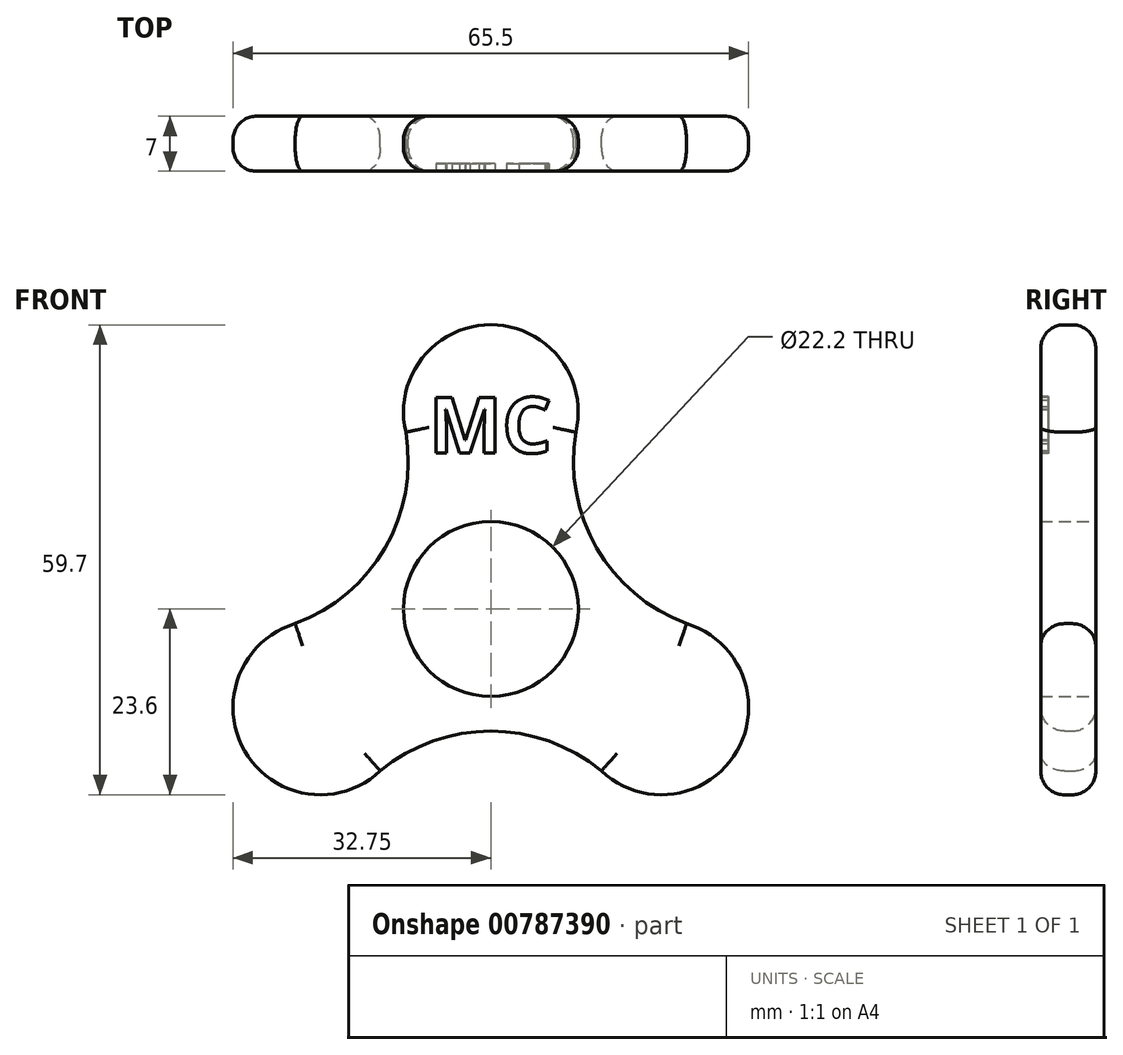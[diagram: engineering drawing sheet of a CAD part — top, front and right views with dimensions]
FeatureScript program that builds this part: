
annotation { "Feature Type Name" : "Feature", "Feature Type Description" : "" }
export const myFeature = defineFeature(function(context is Context, id is Id, definition is map)
    precondition{}
    {
        {
            var Q0;
            Q0=qCreatedBy(makeId("Front.planeOp"),FACE);
            var sketch = newSketch(context, id + "F0", { "sketchPlane" : qUnion([Q0])});
            skCircle(sketch, "E0", {"center": v(0, 0) * mm, "radius": 11.1 * mm});
            skArc(sketch, "E1", {"start": v(10.8, 22.46) * mm, "mid": v(0, 36.1) * mm, "end": v(-10.8, 22.46) * mm});
            skArc(sketch, "E2.1.0", {"start": v(-24.85, -1.87) * mm, "mid": v(-31.26, -18.05) * mm, "end": v(-14.05, -20.59) * mm});
            skArc(sketch, "E2.2.0", {"start": v(14.05, -20.59) * mm, "mid": v(31.26, -18.05) * mm, "end": v(24.85, -1.87) * mm});
            skArc(sketch, "E3", {"start": v(10.8, 22.46) * mm, "mid": v(13.44, 7.76) * mm, "end": v(24.85, -1.87) * mm});
            skArc(sketch, "E4", {"start": v(14.05, -20.59) * mm, "mid": v(0, -15.52) * mm, "end": v(-14.05, -20.59) * mm});
            skArc(sketch, "E5", {"start": v(-24.85, -1.87) * mm, "mid": v(-13.44, 7.76) * mm, "end": v(-10.8, 22.46) * mm});
            skSolve(sketch);
        }
        {
            var Q0;
            Q0 = qSketchRegion(id + "F0", true);
            extrude(context, id + "F1", {"entities" : qUnion([Q0]), "depth" : 7 * mm, "offsetDistance" : 25 * mm});
        }
        {
            var Q0;
            Q0=makeQuery(id+"F1.opExtrude","CAP_EDGE",EDGE,{"disambiguationData":[OSD([sQuery(id+"F0.wireOp",EDGE,"E1")])],"isStart":false});
            var Q1;
            Q1=makeQuery(id+"F1.opExtrude","CAP_EDGE",EDGE,{"disambiguationData":[OSD([sQuery(id+"F0.wireOp",EDGE,"E5")])],"isStart":false});
            var Q2;
            Q2=makeQuery(id+"F1.opExtrude","CAP_EDGE",EDGE,{"disambiguationData":[OSD([sQuery(id+"F0.wireOp",EDGE,"E2.1.0")])],"isStart":false});
            var Q3;
            Q3=makeQuery(id+"F1.opExtrude","CAP_EDGE",EDGE,{"disambiguationData":[OSD([sQuery(id+"F0.wireOp",EDGE,"E4")])],"isStart":false});
            var Q4;
            Q4=makeQuery(id+"F1.opExtrude","CAP_EDGE",EDGE,{"disambiguationData":[OSD([sQuery(id+"F0.wireOp",EDGE,"E2.2.0")])],"isStart":false});
            var Q5;
            Q5=makeQuery(id+"F1.opExtrude","CAP_EDGE",EDGE,{"disambiguationData":[OSD([sQuery(id+"F0.wireOp",EDGE,"E3")])],"isStart":false});
            var Q6;
            Q6=makeQuery(id+"F1.opExtrude","CAP_EDGE",EDGE,{"disambiguationData":[OSD([sQuery(id+"F0.wireOp",EDGE,"E1")])],"isStart":true});
            var Q7;
            Q7=makeQuery(id+"F1.opExtrude","CAP_EDGE",EDGE,{"disambiguationData":[OSD([sQuery(id+"F0.wireOp",EDGE,"E5")])],"isStart":true});
            var Q8;
            Q8=makeQuery(id+"F1.opExtrude","CAP_EDGE",EDGE,{"disambiguationData":[OSD([sQuery(id+"F0.wireOp",EDGE,"E2.1.0")])],"isStart":true});
            var Q9;
            Q9=makeQuery(id+"F1.opExtrude","CAP_EDGE",EDGE,{"disambiguationData":[OSD([sQuery(id+"F0.wireOp",EDGE,"E4")])],"isStart":true});
            var Q10;
            Q10=makeQuery(id+"F1.opExtrude","CAP_EDGE",EDGE,{"disambiguationData":[OSD([sQuery(id+"F0.wireOp",EDGE,"E2.2.0")])],"isStart":true});
            fillet(context, id + "F2", {"entities" : qUnion([Q0, Q1, Q2, Q3, Q4, Q5, Q6, Q7, Q8, Q9, Q10]), "radius" : 3 * mm, "tangentPropagation" : true, "allowEdgeOverflow" : false});
        }
        {
            var Q0;
            Q0=makeQuery(id+"F1.opExtrude","CAP_FACE",FACE,{"disambiguationData":[OSD([sQuery(id+"F0.wireOp",EDGE,"E0"),sQuery(id+"F0.wireOp",EDGE,"E1"),sQuery(id+"F0.wireOp",EDGE,"E2.1.0"),sQuery(id+"F0.wireOp",EDGE,"E2.2.0"),sQuery(id+"F0.wireOp",EDGE,"E3"),sQuery(id+"F0.wireOp",EDGE,"E4"),sQuery(id+"F0.wireOp",EDGE,"E5")])],"isStart":false});
            var sketch = newSketch(context, id + "F3", { "sketchPlane" : qUnion([Q0])});
            skText(sketch, "E6", { "text": "MC", "fontName": "OpenSans-Bold.ttf"});
            const initialGuessF3  = {"E6": [-0.00787, 0.01982, 1, 0, 0.00711]};
            skSetInitialGuess(sketch, initialGuessF3);
            skSolve(sketch);
        }
        {
            var Q0;
            Q0 = qSketchRegion(id + "F3", true);
            extrude(context, id + "F4", {"entities" : qUnion([Q0]), "operationType" : NewBodyOperationType.REMOVE, "oppositeDirection" : true, "depth" : 1 * mm, "offsetDistance" : 25 * mm});
        }
    });
